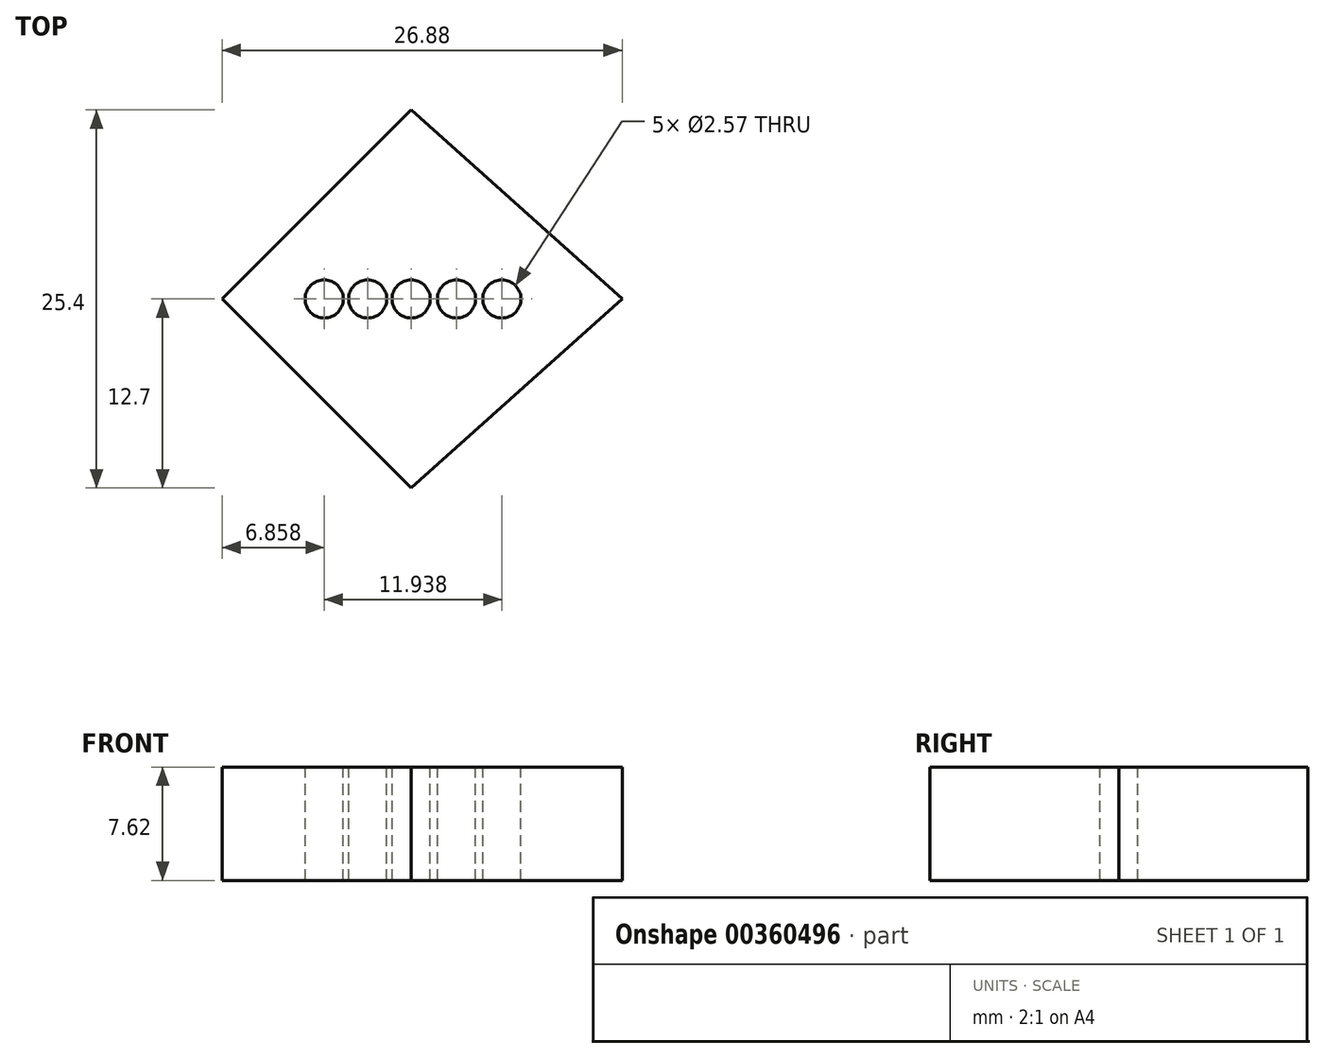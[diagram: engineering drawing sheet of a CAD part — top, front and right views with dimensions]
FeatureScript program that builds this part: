
annotation { "Feature Type Name" : "Feature", "Feature Type Description" : "" }
export const myFeature = defineFeature(function(context is Context, id is Id, definition is map)
    precondition{}
    {
        {
            var Q0;
            Q0=qCreatedBy(makeId("Top.planeOp"),FACE);
            var sketch = newSketch(context, id + "F0", { "sketchPlane" : qUnion([Q0])});
            skLineSegment(sketch, "E0", {"start": v(0, 12.7) * mm, "end": v(0, -12.7) * mm, "construction": true});
            skLineSegment(sketch, "E1", {"start": v(-12.7, 0) * mm, "end": v(14.18, 0) * mm, "construction": true});
            skLineSegment(sketch, "E2", {"start": v(0, 12.7) * mm, "end": v(-12.7, 0) * mm});
            skLineSegment(sketch, "E3", {"start": v(-12.7, 0) * mm, "end": v(0, -12.7) * mm});
            skLineSegment(sketch, "E4", {"start": v(0, 12.7) * mm, "end": v(14.18, 0) * mm});
            skLineSegment(sketch, "E5", {"start": v(14.18, 0) * mm, "end": v(0, -12.7) * mm});
            skSolve(sketch);
        }
        {
            var Q0;
            Q0=makeQuery(id+"F0.imprint","IMPRINT",FACE,{"disambiguationData":[TD([[makeQuery(id+"F0.imprint","IMPRINT",EDGE,{"derivedFrom":sQuery(id+"F0.wireOp",EDGE,"E2")}),1.0]])]});
            extrude(context, id + "F1", {"entities" : qUnion([Q0]), "depth" : 7.62 * mm});
        }
        {
            var Q0;
            Q0=makeQuery(id+"F1.opExtrude","CAP_FACE",FACE,{"disambiguationData":[OSD([sQuery(id+"F0.wireOp",EDGE,"E2"),sQuery(id+"F0.wireOp",EDGE,"E3"),sQuery(id+"F0.wireOp",EDGE,"E4"),sQuery(id+"F0.wireOp",EDGE,"E5")])],"isStart":false});
            var sketch = newSketch(context, id + "F2", { "sketchPlane" : qUnion([Q0])});
            skCircle(sketch, "E6", {"center": v(0, 0) * mm, "radius": 1.28 * mm});
            skCircle(sketch, "E7.1.0.0", {"center": v(3.05, 0) * mm, "radius": 1.28 * mm});
            skLineSegment(sketch, "E7.direction1", {"start": v(0, 0) * mm, "end": v(3.05, 0) * mm, "construction": true});
            skCircle(sketch, "E8.0.2.0", {"center": v(6.1, 0) * mm, "radius": 1.28 * mm});
            skCircle(sketch, "E9.1.0.0", {"center": v(-2.92, 0) * mm, "radius": 1.28 * mm});
            skCircle(sketch, "E9.2.0.0", {"center": v(-5.84, 0) * mm, "radius": 1.28 * mm});
            skLineSegment(sketch, "E9.direction1", {"start": v(0, 0) * mm, "end": v(-2.92, 0) * mm, "construction": true});
            skCircle(sketch, "E10.1.0.0", {"center": v(19.3, 0) * mm, "radius": 1.28 * mm});
            skCircle(sketch, "E10.2.0.0", {"center": v(38.6, 0) * mm, "radius": 1.28 * mm});
            skLineSegment(sketch, "E10.direction1", {"start": v(0, 0) * mm, "end": v(19.3, 0) * mm, "construction": true});
            skSolve(sketch);
        }
        {
            var Q0;
            Q0=makeQuery(id+"F2.imprint","IMPRINT",FACE,{"disambiguationData":[TD([[makeQuery(id+"F2.imprint","IMPRINT",EDGE,{"derivedFrom":sQuery(id+"F2.wireOp",EDGE,"E9.2.0.0")}),1.0]])]});
            var Q1;
            Q1=makeQuery(id+"F2.imprint","IMPRINT",FACE,{"disambiguationData":[TD([[makeQuery(id+"F2.imprint","IMPRINT",EDGE,{"derivedFrom":sQuery(id+"F2.wireOp",EDGE,"E9.1.0.0")}),1.0]])]});
            var Q2;
            Q2=makeQuery(id+"F2.imprint","IMPRINT",FACE,{"disambiguationData":[TD([[makeQuery(id+"F2.imprint","IMPRINT",EDGE,{"derivedFrom":sQuery(id+"F2.wireOp",EDGE,"E6")}),1.0]])]});
            var Q3;
            Q3=makeQuery(id+"F2.imprint","IMPRINT",FACE,{"disambiguationData":[TD([[makeQuery(id+"F2.imprint","IMPRINT",EDGE,{"derivedFrom":sQuery(id+"F2.wireOp",EDGE,"E7.1.0.0")}),1.0]])]});
            var Q4;
            Q4=makeQuery(id+"F2.imprint","IMPRINT",FACE,{"disambiguationData":[TD([[makeQuery(id+"F2.imprint","IMPRINT",EDGE,{"derivedFrom":sQuery(id+"F2.wireOp",EDGE,"E8.0.2.0")}),1.0]])]});
            extrude(context, id + "F3", {"entities" : qUnion([Q0, Q1, Q2, Q3, Q4]), "operationType" : NewBodyOperationType.REMOVE, "endBound" : BoundingType.THROUGH_ALL, "oppositeDirection" : true, "depth" : 25.4 * mm});
        }
    });
